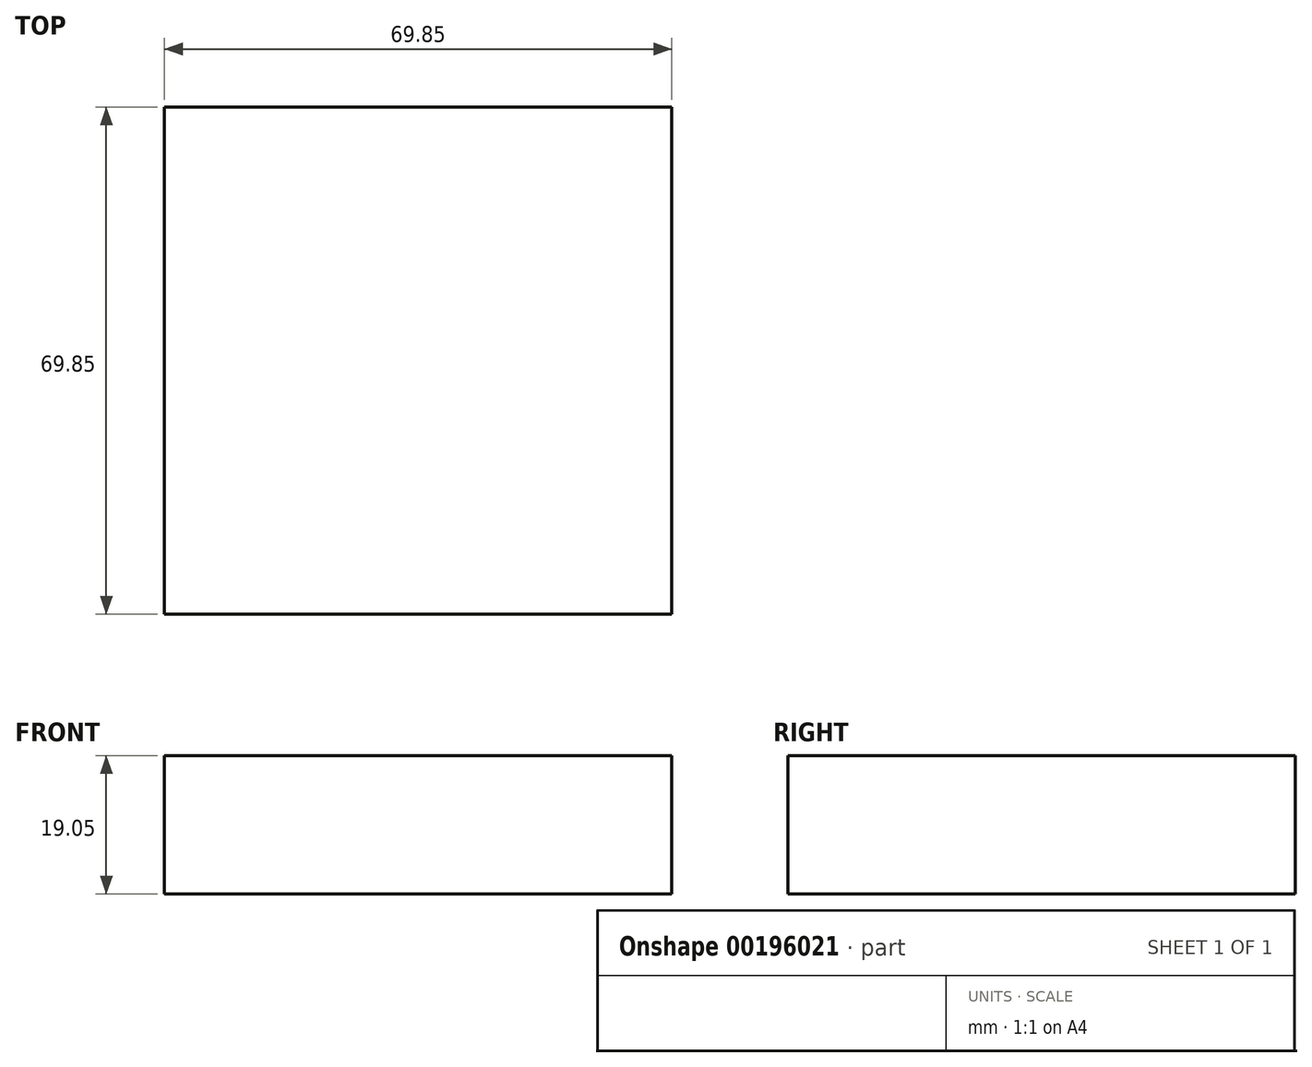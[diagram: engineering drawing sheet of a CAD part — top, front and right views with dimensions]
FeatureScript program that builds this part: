
annotation { "Feature Type Name" : "Feature", "Feature Type Description" : "" }
export const myFeature = defineFeature(function(context is Context, id is Id, definition is map)
    precondition{}
    {
        {
            var Q0;
            Q0=qCreatedBy(makeId("Top.planeOp"),FACE);
            var sketch = newSketch(context, id + "F0", { "sketchPlane" : qUnion([Q0])});
            skLineSegment(sketch, "E0.bottom", {"start": v(-35.53, 35.6) * mm, "end": v(34.32, 35.6) * mm});
            skLineSegment(sketch, "E0.top", {"start": v(-35.53, -34.25) * mm, "end": v(34.32, -34.25) * mm});
            skLineSegment(sketch, "E0.left", {"start": v(-35.53, 35.6) * mm, "end": v(-35.53, -34.25) * mm});
            skLineSegment(sketch, "E0.right", {"start": v(34.32, 35.6) * mm, "end": v(34.32, -34.25) * mm});
            skSolve(sketch);
        }
        {
            var Q0;
            Q0=makeQuery(id+"F0.imprint","IMPRINT",FACE,{"disambiguationData":[TD([[makeQuery(id+"F0.imprint","IMPRINT",EDGE,{"derivedFrom":sQuery(id+"F0.wireOp",EDGE,"E0.bottom")}),-1.0]])]});
            extrude(context, id + "F1", {"entities" : qUnion([Q0]), "depth" : 19.05 * mm});
        }
    });
